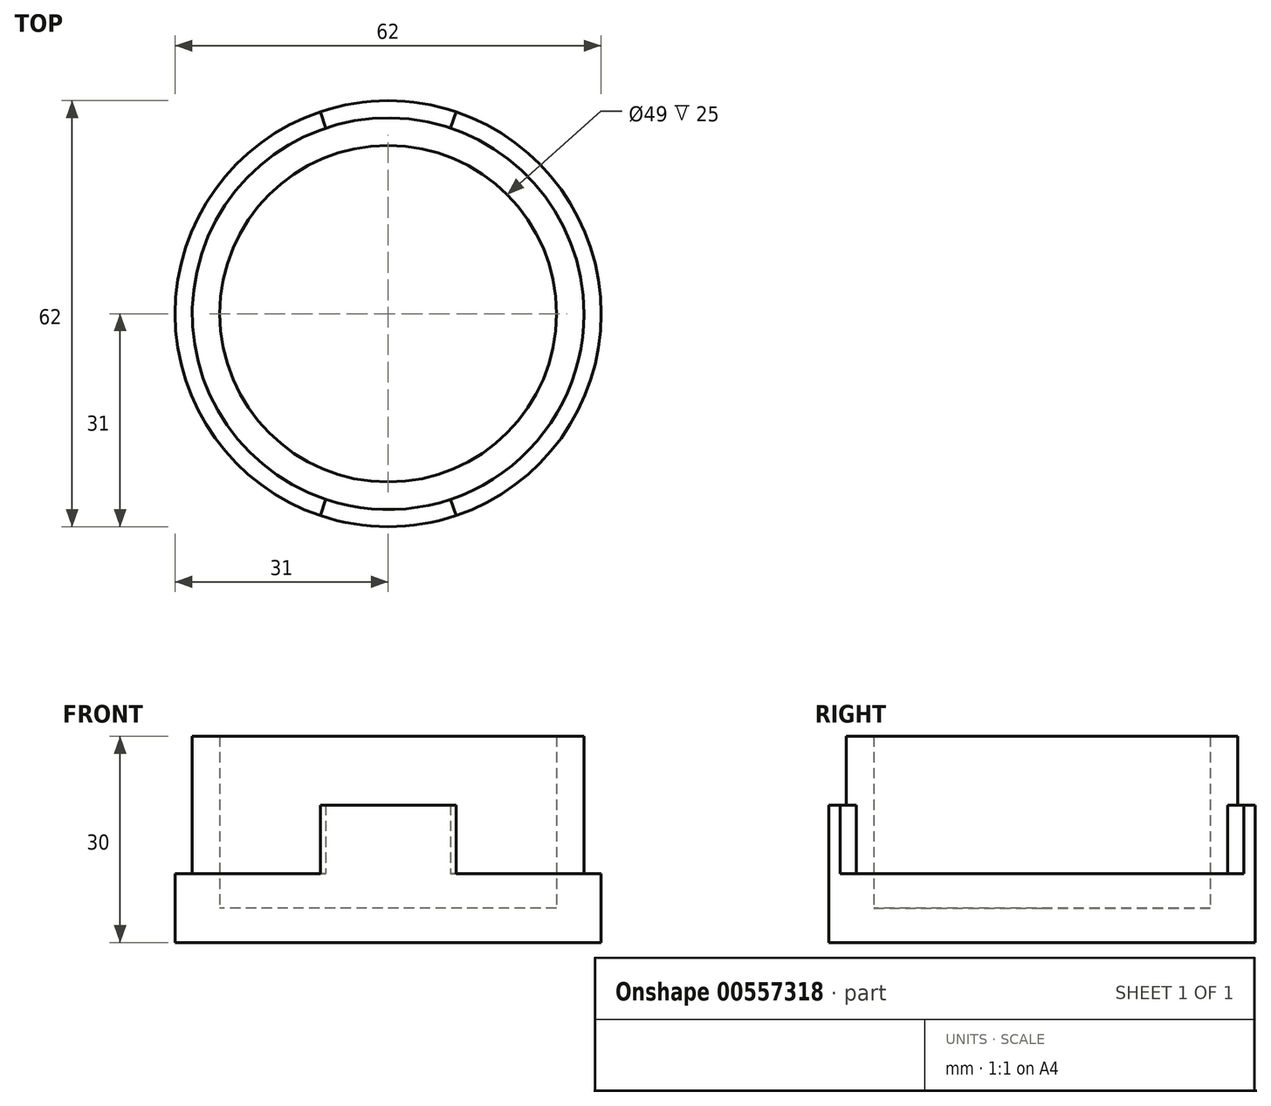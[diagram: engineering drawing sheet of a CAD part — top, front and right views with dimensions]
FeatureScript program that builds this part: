
annotation { "Feature Type Name" : "Feature", "Feature Type Description" : "" }
export const myFeature = defineFeature(function(context is Context, id is Id, definition is map)
    precondition{}
    {
        {
            var Q0;
            Q0=qCreatedBy(makeId("Top.planeOp"),FACE);
            var sketch = newSketch(context, id + "F0", { "sketchPlane" : qUnion([Q0])});
            skCircle(sketch, "E0", {"center": v(0, 0) * mm, "radius": 28.5 * mm});
            skCircle(sketch, "E1", {"center": v(0, 0) * mm, "radius": 24.5 * mm});
            skCircle(sketch, "E2", {"center": v(0, 0) * mm, "radius": 31 * mm});
            skLineSegment(sketch, "E3", {"start": v(9.87, 29.39) * mm, "end": v(9.07, 27.02) * mm});
            skLineSegment(sketch, "E4.MirrorCS", {"start": v(-9.87, 29.39) * mm, "end": v(-9.07, 27.02) * mm});
            skLineSegment(sketch, "E5.left", {"start": v(-9.07, 27.02) * mm, "end": v(-9.07, 27.02) * mm});
            skLineSegment(sketch, "E5.right", {"start": v(9.07, 27.02) * mm, "end": v(9.07, 27.02) * mm});
            skLineSegment(sketch, "E6.left", {"start": v(-9.87, 29.39) * mm, "end": v(-9.87, 29.39) * mm});
            skLineSegment(sketch, "E6.right", {"start": v(9.87, 29.39) * mm, "end": v(9.87, 29.39) * mm});
            skLineSegment(sketch, "E7", {"start": v(-9.07, -27.02) * mm, "end": v(-9.87, -29.39) * mm});
            skLineSegment(sketch, "E8", {"start": v(9.07, -27.02) * mm, "end": v(9.87, -29.39) * mm});
            skSolve(sketch);
        }
        {
            var Q0;
            Q0=makeQuery(id+"F0.imprint","IMPRINT",FACE,{"disambiguationData":[TD([[makeQuery(id+"F0.imprint","IMPRINT",EDGE,{"derivedFrom":sQuery(id+"F0.wireOp",EDGE,"E0")}),-1.0]])]});
            extrude(context, id + "F1", {"entities" : qUnion([Q0]), "depth" : 10 * mm, "offsetDistance" : 25 * mm});
        }
        {
            var Q0;
            Q0=makeQuery(id+"F0.imprint","IMPRINT",FACE,{"disambiguationData":[TD([[makeQuery(id+"F0.imprint","IMPRINT",EDGE,{"derivedFrom":sQuery(id+"F0.wireOp",EDGE,"E0")}),1.0]])]});
            extrude(context, id + "F2", {"entities" : qUnion([Q0]), "operationType" : NewBodyOperationType.REMOVE, "depth" : 30 * mm, "offsetDistance" : 25 * mm});
        }
        {
            var Q0;
            {var subQ0=sQuery(id+"F0.wireOp",EDGE,"E3");Q0=makeQuery(id+"F0.imprint","IMPRINT",FACE,{"disambiguationData":[TD([[makeQuery(id+"F0.imprint","IMPRINT",EDGE,{"derivedFrom":subQ0}),-1.0]])]});}
            extrude(context, id + "F3", {"entities" : qUnion([Q0]), "operationType" : NewBodyOperationType.ADD, "depth" : 20 * mm, "offsetDistance" : 25 * mm});
        }
        {
            var Q0;
            {var subQ0=sQuery(id+"F0.wireOp",EDGE,"E7");Q0=makeQuery(id+"F0.imprint","IMPRINT",FACE,{"disambiguationData":[TD([[makeQuery(id+"F0.imprint","IMPRINT",EDGE,{"derivedFrom":subQ0}),1.0]])]});}
            extrude(context, id + "F4", {"entities" : qUnion([Q0]), "operationType" : NewBodyOperationType.ADD, "depth" : 20 * mm, "offsetDistance" : 25 * mm});
        }
        {
            var Q0;
            Q0=makeQuery(id+"F0.imprint","IMPRINT",FACE,{"disambiguationData":[TD([[makeQuery(id+"F0.imprint","IMPRINT",EDGE,{"derivedFrom":sQuery(id+"F0.wireOp",EDGE,"E1")}),-1.0]])]});
            extrude(context, id + "F5", {"entities" : qUnion([Q0]), "operationType" : NewBodyOperationType.ADD, "depth" : 30 * mm, "offsetDistance" : 25 * mm});
        }
        {
            var Q0;
            Q0=makeQuery(id+"F0.imprint","IMPRINT",FACE,{"disambiguationData":[TD([[makeQuery(id+"F0.imprint","IMPRINT",EDGE,{"derivedFrom":sQuery(id+"F0.wireOp",EDGE,"E1")}),1.0]])]});
            extrude(context, id + "F6", {"entities" : qUnion([Q0]), "operationType" : NewBodyOperationType.ADD, "depth" : 5 * mm, "offsetDistance" : 25 * mm});
        }
    });
